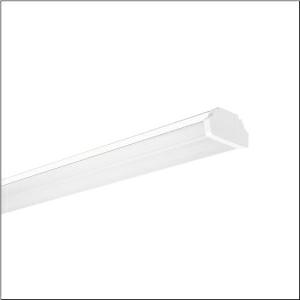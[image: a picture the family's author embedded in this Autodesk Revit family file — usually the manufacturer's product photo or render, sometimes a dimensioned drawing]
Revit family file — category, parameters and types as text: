
# Revit family: dus_r__31_mo_53bd812c1v6075_124e
name_source: partatom
category: Lighting Fixtures
units: mm (PartAtom-declared; Revit-internal decimal feet)

## family parameters
Cut with Voids When Loaded = No
Host = Face
Light Source = No
Part Type = Normal
Room Calculation Point = No
Round Connector Dimension = Use Diameter
Shared = No

## types (1)
- --- (1 x LED, 7640 lm, 48.9 W, 6500K)
    Apparent Load = 49 VA
    CIE Flux Codes = 47 80 95 92 100
    Color Rendering = 80
    Color Temperature = 6500K
    Default Elevation = 1800 mm
    Description = DUS® 31 MO, luminaire insert, of sheet steel, coil coated, white, length: 1.535mm, width: 81mm, height: 90mm, 5x system unit, system units: 307mm, LED rated luminous flux: 7.640lm, light colour: 865, control gear: ON/OFF Multilumen, CLOi, control gear: ECG Multilumen, with plug, 3-pole, with phase selection, mains connection: 220..240V, AC, 50/60Hz, start of lifetime: 49W, end of service life: 56W, through-wiring accessed according to module size, primary optical cover: cover, of PMMA, light emission: direct distribution, primary light characteristic: symmetric, protection rating (complete): IP20, protection rating (LED compartment): IP50, insulation class (complete): insulation class I (protective earthing), certification: CE, ENEC, VDE, UKCA, impact resistance: IK03, permissible ambient temperature for indoor applications: -35..+30°C, corresponds to IFS (International Featured Standards) requirements for safety and quality in the food industry, reducing of maximum allowable ambient temperature of 5°C with ceiling mounting, packaging unit: 1 piece
    Height = 95 mm
    Lamp = 1 x LED
    Lamp Light Flux = 7640 lm
    Lamp Power = 48.9 W
    Lamp count = 1
    Length = 1535 mm
    Luminous efficacy = 156 lm/W
    Manufacturer = Siteco
    ModVariant = No
    Model = 53BD812C1V6075
    Mounting Place = Ceiling
    Mounting Type = Pendant
    Number of Poles = 1
    OnlyDefault = Yes
    Power Factor = 1
    Product Name = DUS® 31 MO
    Product group = luminaire insert
    ProductGroupID = 901
    Protection Class = Protection class I
    Protection Degree = IP 20
    RLX_Detail_Level = 1
    RLX_Emergency_Light_Flux = 0 lm
    RLX_Emergency_Type = 0
    RLX_Emergency_Type_DB = No
    RlxData = <blob elided: 39821 chars, md5=146d94c2>
    Socket = socket
    Standby Power = 0 W
    System Light Flux = 7640 lm
    System Power = 49 W
    Type Comments = factory setting: luminous flux: 100 % | (A | C | E) | 107 mA
    Type Image = l_1313537.jpg
    URL = http://relux.com
    VarID = @adj_154971
    Voltage = 0 V
    Weight = 0.00 kg
    Width = 81 mm

## geometry (parser evidence)
native form markers: Blend x4, Sweep x12
no freeform markers — native parametric forms only
